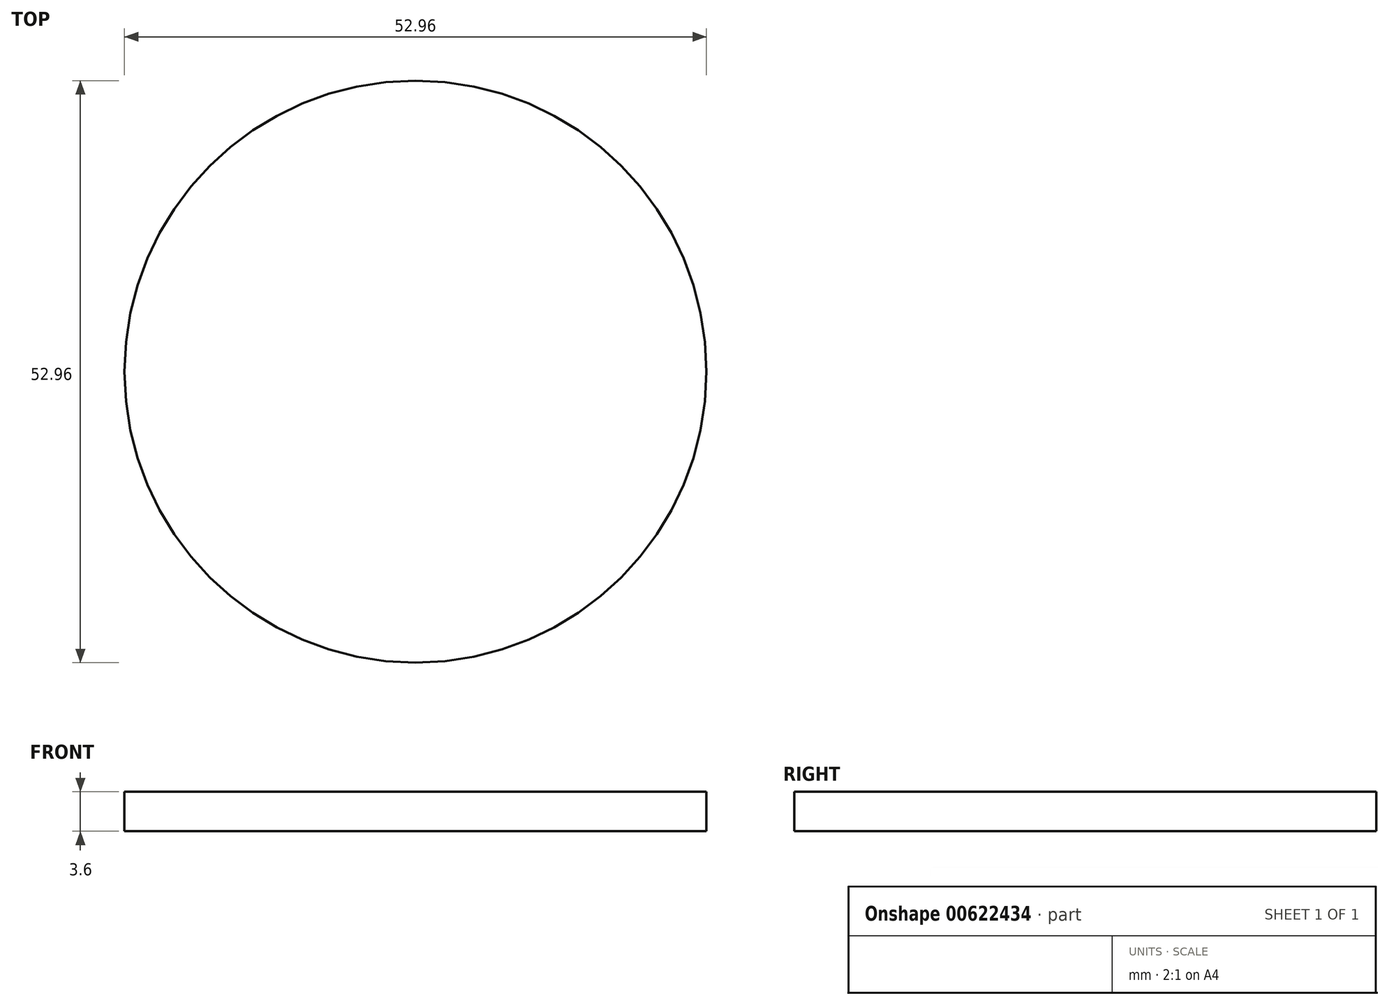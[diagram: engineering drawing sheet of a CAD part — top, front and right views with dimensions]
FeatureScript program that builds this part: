
annotation { "Feature Type Name" : "Feature", "Feature Type Description" : "" }
export const myFeature = defineFeature(function(context is Context, id is Id, definition is map)
    precondition{}
    {
        {
            var Q0;
            Q0=qCreatedBy(makeId("Top.planeOp"),FACE);
            var sketch = newSketch(context, id + "F0", { "sketchPlane" : qUnion([Q0])});
            skCircle(sketch, "E0", {"center": v(0, 0) * mm, "radius": 28.29 * mm});
            skCircle(sketch, "E1", {"center": v(0, 0) * mm, "radius": 26.48 * mm});
            skSolve(sketch);
        }
        {
            var Q0;
            Q0=makeQuery(id+"F0.imprint","IMPRINT",FACE,{"disambiguationData":[TD([[makeQuery(id+"F0.imprint","IMPRINT",EDGE,{"derivedFrom":sQuery(id+"F0.wireOp",EDGE,"E1")}),1.0]])]});
            extrude(context, id + "F1", {"entities" : qUnion([Q0]), "oppositeDirection" : true, "depth" : 1.8 * mm, "offsetDistance" : 25.4 * mm, "hasSecondDirection" : true, "secondDirectionOppositeDirection" : false, "secondDirectionDepth" : 1.8 * mm});
        }
    });
